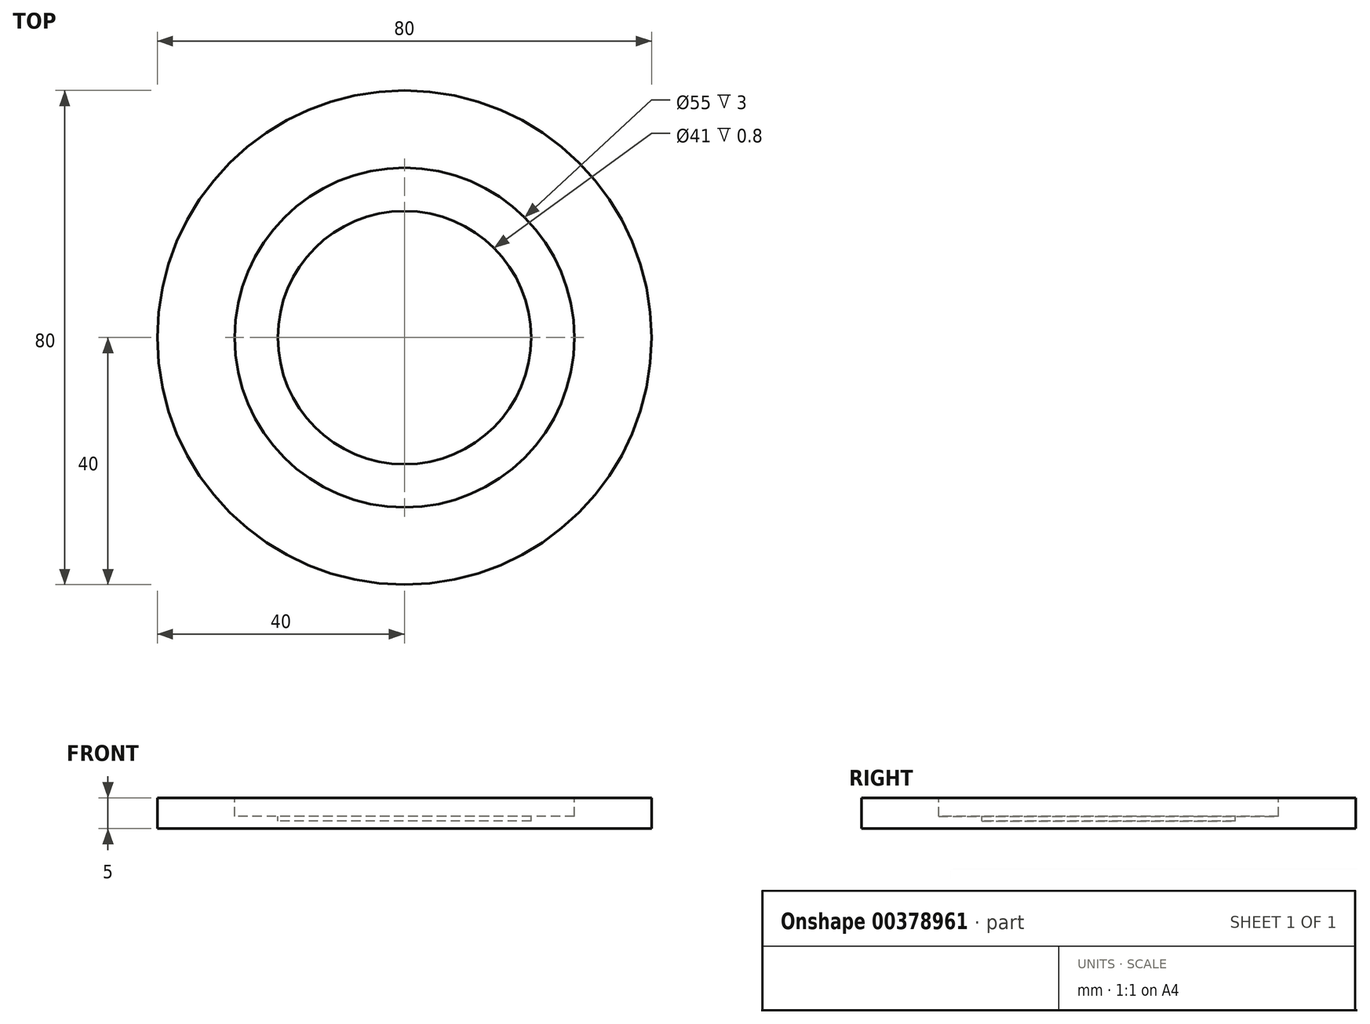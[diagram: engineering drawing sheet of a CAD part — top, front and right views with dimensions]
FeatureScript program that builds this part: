
annotation { "Feature Type Name" : "Feature", "Feature Type Description" : "" }
export const myFeature = defineFeature(function(context is Context, id is Id, definition is map)
    precondition{}
    {
        {
            var Q0;
            Q0=qCreatedBy(makeId("Top.planeOp"),FACE);
            var sketch = newSketch(context, id + "F0", { "sketchPlane" : qUnion([Q0])});
            skCircle(sketch, "E0", {"center": v(0, 0) * mm, "radius": 40 * mm});
            skSolve(sketch);
        }
        {
            var Q0;
            Q0 = qSketchRegion(id + "F0", true);
            extrude(context, id + "F1", {"entities" : qUnion([Q0]), "depth" : 5 * mm});
        }
        {
            var Q0;
            Q0=makeQuery(id+"F1.opExtrude","CAP_FACE",FACE,{"disambiguationData":[OSD([sQuery(id+"F0.wireOp",EDGE,"E0")])],"isStart":false});
            var sketch = newSketch(context, id + "F2", { "sketchPlane" : qUnion([Q0])});
            skCircle(sketch, "E1", {"center": v(0, 0) * mm, "radius": 27.5 * mm});
            skSolve(sketch);
        }
        {
            var Q0;
            Q0 = qSketchRegion(id + "F2", true);
            extrude(context, id + "F3", {"entities" : qUnion([Q0]), "operationType" : NewBodyOperationType.REMOVE, "oppositeDirection" : true, "depth" : 3 * mm});
        }
        {
            var Q0;
            Q0=makeQuery(id+"F3.boolean.opBoolean","COPY",FACE,{"derivedFrom":makeQuery(id+"F3.opExtrude","CAP_FACE",FACE,{"disambiguationData":[OSD([sQuery(id+"F2.wireOp",EDGE,"E1")])],"isStart":false})});
            var sketch = newSketch(context, id + "F4", { "sketchPlane" : qUnion([Q0])});
            skCircle(sketch, "E2", {"center": v(0, 0) * mm, "radius": 20.5 * mm});
            skSolve(sketch);
        }
        {
            var Q0;
            Q0 = qSketchRegion(id + "F4", true);
            extrude(context, id + "F5", {"entities" : qUnion([Q0]), "operationType" : NewBodyOperationType.REMOVE, "oppositeDirection" : true, "depth" : .8 * mm});
        }
    });
